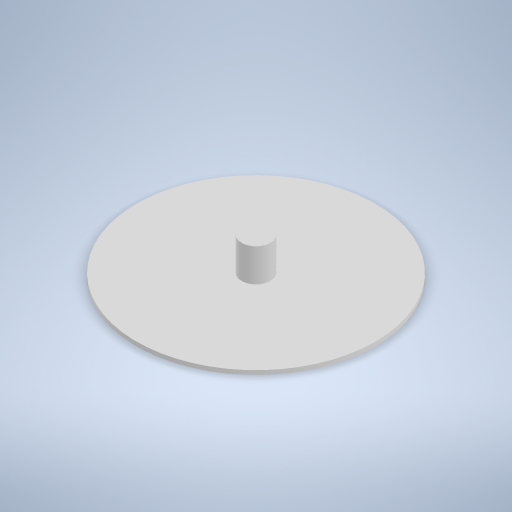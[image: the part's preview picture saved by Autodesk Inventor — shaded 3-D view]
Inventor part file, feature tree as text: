
AUTODESK INVENTOR PART (.ipt)
format: ipt  version: 2024 (Build 280153000, 153)  size: 225,280 bytes
history: native  units: mm
features: extrude x2, sketch x2
ambient origin geometry x8: Origin, YZ Plane, XZ Plane, XY Plane, X Axis, Y Axis, Z Axis, Center Point
bodies: Volumenkörper1 (feature_tree)
feature tree (4):
  extrude  "Extrusion1"  Depth=0.5mm TaperAngle=0.0deg
  extrude  "Extrusion2"  Depth=4.0mm TaperAngle=0.0deg
  sketch  "Skizze1"  dims[d0=29.0mm d1=0.5mm d2=0.0mm]
  sketch  "Skizze2"  dims[d3=3.5mm d4=4.0mm d5=0.0mm]
